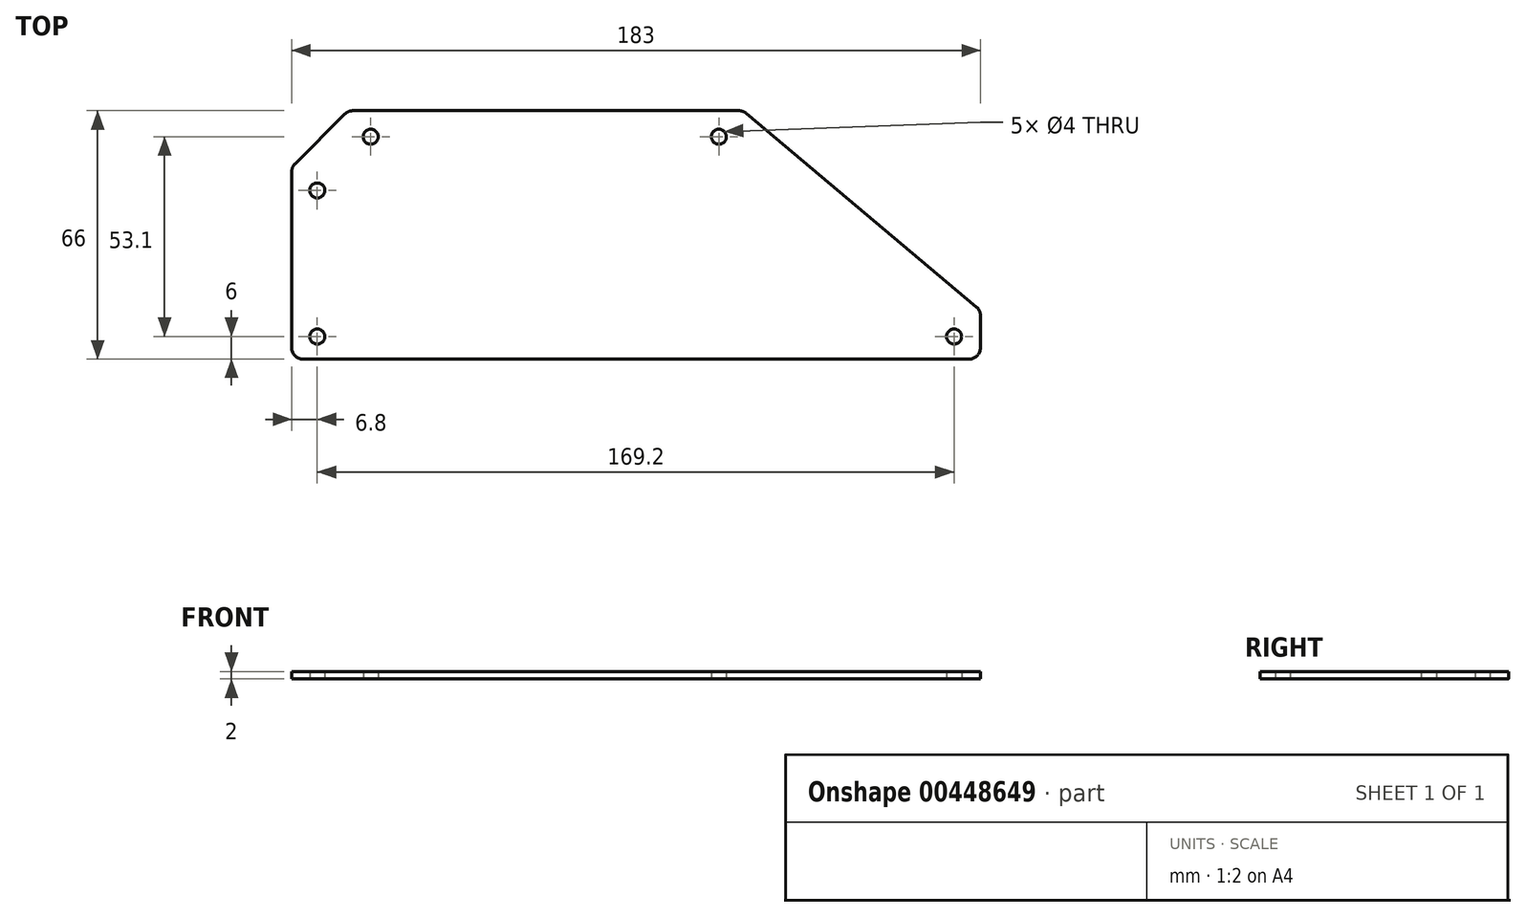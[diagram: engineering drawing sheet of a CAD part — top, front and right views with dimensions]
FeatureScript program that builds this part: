
annotation { "Feature Type Name" : "Feature", "Feature Type Description" : "" }
export const myFeature = defineFeature(function(context is Context, id is Id, definition is map)
    precondition{}
    {
        {
            var Q0;
            Q0=qCreatedBy(makeId("Top.planeOp"),FACE);
            var sketch = newSketch(context, id + "F0", { "sketchPlane" : qUnion([Q0])});
            skCircle(sketch, "E0", {"center": v(-84.7, -27) * mm, "radius": 2 * mm});
            skCircle(sketch, "E1", {"center": v(84.5, -27) * mm, "radius": 2 * mm});
            skCircle(sketch, "E2", {"center": v(-84.7, 11.8) * mm, "radius": 2 * mm});
            skLineSegment(sketch, "E3", {"start": v(90.43, -19.1) * mm, "end": v(29.34, 32.3) * mm});
            skArc(sketch, "E4", {"start": v(29.34, 32.3) * mm, "mid": v(28.43, 32.82) * mm, "end": v(27.4, 33) * mm});
            skLineSegment(sketch, "E5", {"start": v(-75.26, 33) * mm, "end": v(27.4, 33) * mm});
            skArc(sketch, "E6", {"start": v(-75.26, 33) * mm, "mid": v(-76.4, 32.77) * mm, "end": v(-77.38, 32.12) * mm});
            skLineSegment(sketch, "E7", {"start": v(-90.62, 18.88) * mm, "end": v(-77.38, 32.12) * mm});
            skArc(sketch, "E8", {"start": v(-90.62, 18.88) * mm, "mid": v(-91.27, 17.9) * mm, "end": v(-91.5, 16.76) * mm});
            skLineSegment(sketch, "E9", {"start": v(-91.5, -30) * mm, "end": v(-91.5, 16.76) * mm});
            skArc(sketch, "E10", {"start": v(-91.5, -30) * mm, "mid": v(-90.62, -32.12) * mm, "end": v(-88.5, -33) * mm});
            skLineSegment(sketch, "E11", {"start": v(-88.5, -33) * mm, "end": v(88.5, -33) * mm});
            skArc(sketch, "E12", {"start": v(88.5, -33) * mm, "mid": v(90.62, -32.12) * mm, "end": v(91.5, -30) * mm});
            skLineSegment(sketch, "E13", {"start": v(91.5, -30) * mm, "end": v(91.5, -21.4) * mm});
            skArc(sketch, "E14", {"start": v(91.5, -21.4) * mm, "mid": v(91.22, -20.13) * mm, "end": v(90.43, -19.1) * mm});
            skCircle(sketch, "E15", {"center": v(-70.5, 26.1) * mm, "radius": 2 * mm});
            skCircle(sketch, "E16", {"center": v(22, 26.1) * mm, "radius": 2 * mm});
            skSolve(sketch);
        }
        {
            var Q0;
            Q0=makeQuery(id+"F0.imprint","IMPRINT",FACE,{"disambiguationData":[TD([[makeQuery(id+"F0.imprint","IMPRINT",EDGE,{"derivedFrom":sQuery(id+"F0.wireOp",EDGE,"E0")}),-1.0]])]});
            extrude(context, id + "F1", {"entities" : qUnion([Q0]), "depth" : 2 * mm});
        }
    });
